# Revit family: QF_MACOM_HOSDCM120KE-2M
name_source: partatom
category: Specialty Equipment
units: mm (PartAtom-declared; Revit-internal decimal feet)

## family parameters
Always vertical = Yes
Cut with Voids When Loaded = No
OmniClass Number = 23.40.40.14.27
OmniClass Title = Ice Machines
Part Type = Normal
Room Calculation Point = No
Round Connector Dimension = Use Diameter
Shared = No
Work Plane-Based = No

## types (1)
- HOSDCM120KE-2M
    Cold Water Connection Height = 0 mm
    Cold Water Flow = 0,0 L/s
    Cold Water Maximum Pressure = 0,0 Pa
    Cold Water Minimum Pressure = 0,0 Pa
    Cold Water RI Height = 0 mm
    Cold Water Size = 3/4"
    Cold Water Temperature Recommended = -273 °C
    Conn Conduit = Yes
    Default Elevation = 0 mm
    Description = MAQUINA DE GELO CUBELET HOSHIZAKI PRODUCAO ATE 102KG/DIA COM DISPENSADOR P/AUTO SERVICO E DEPOSITO PARA 4KG - 220V MONOF-350X585X815
    Elec Conn RI Height = 0 mm
    FL Amps = 0 A
    Indirect Waste Connection Height = 0 mm
    Indirect Waste Flow = 0,0 L/s
    Indirect Waste Size = 25,00 mm
    Manufacturer = MACOM
    Max Overcurrent Protection = 0 A
    Min Ckt Ampacity = 0 A
    Model = HOSDCM120KE-2M
    Number of Poles = 0
    Production per Cycle = 230 cubes
    Production per day = 85kG to 125Kg
    Storage = 4,00 kg
    URL = https://www.acosmacom.com.br
    Waste Water Discharge Temperature = -273 °C
    Water Consumption per day = 85L to 125L

## geometry (parser evidence)
native form markers: Blend x4, Sweep x5
no freeform markers — native parametric forms only
